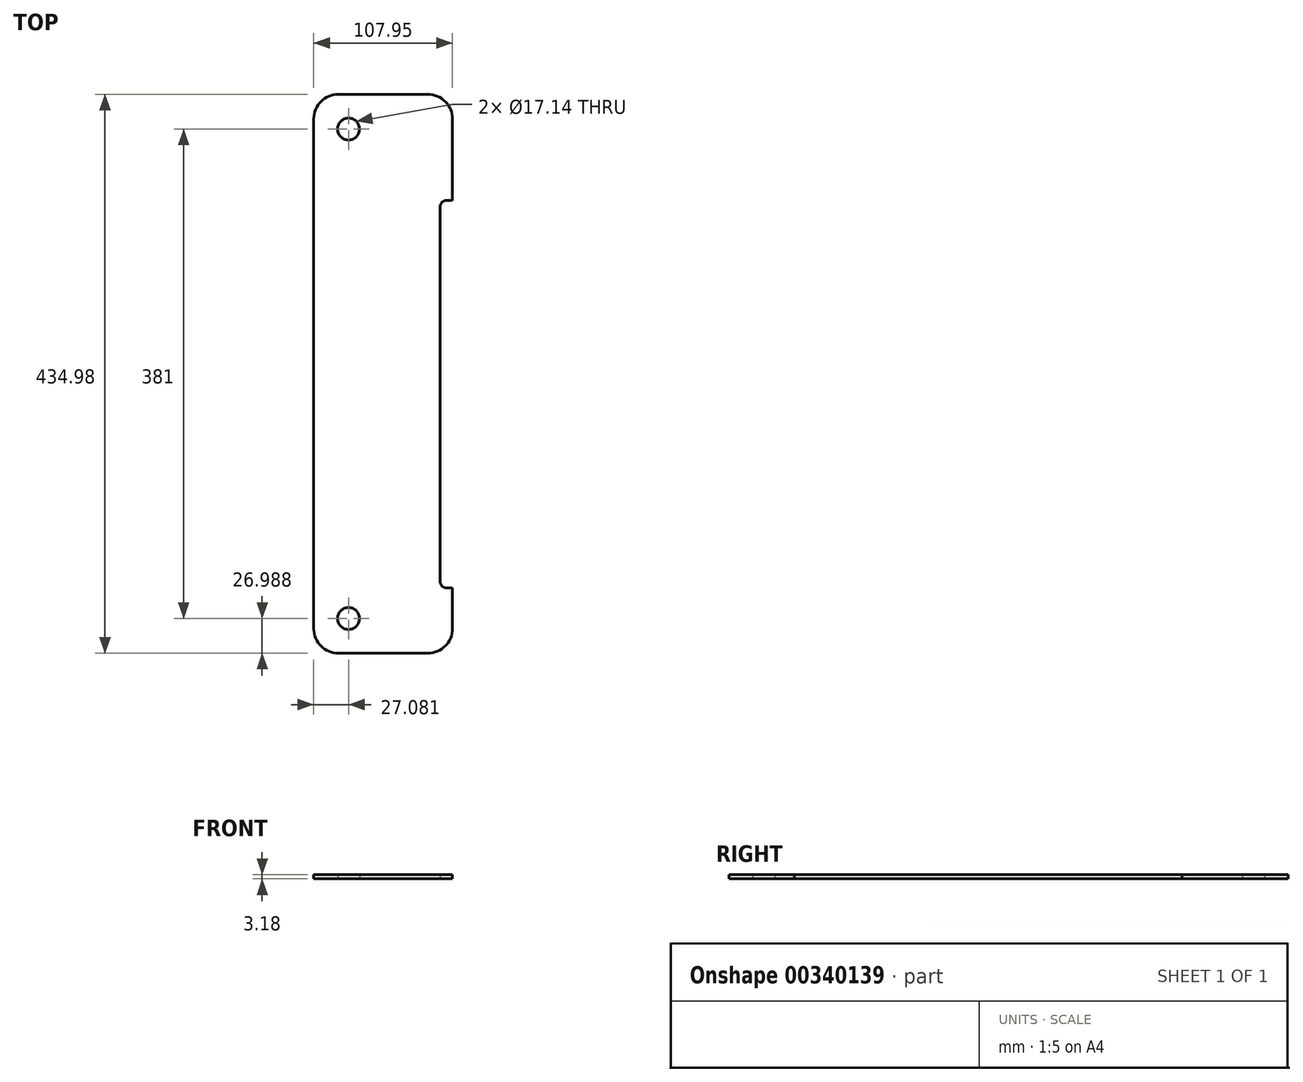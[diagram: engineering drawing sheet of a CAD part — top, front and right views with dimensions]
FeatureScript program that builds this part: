
annotation { "Feature Type Name" : "Feature", "Feature Type Description" : "" }
export const myFeature = defineFeature(function(context is Context, id is Id, definition is map)
    precondition{}
    {
        {
            var Q0;
            Q0=qCreatedBy(makeId("Top.planeOp"),FACE);
            var sketch = newSketch(context, id + "F0", { "sketchPlane" : qUnion([Q0])});
            skLineSegment(sketch, "E0.bottom", {"start": v(-130.08, 214.6) * mm, "end": v(-22.13, 214.6) * mm});
            skLineSegment(sketch, "E0.top", {"start": v(-130.08, -220.38) * mm, "end": v(-22.13, -220.38) * mm});
            skLineSegment(sketch, "E0.left", {"start": v(-130.08, 214.6) * mm, "end": v(-130.08, -220.38) * mm});
            skLineSegment(sketch, "E0.right", {"start": v(-22.13, 214.6) * mm, "end": v(-22.13, 132.05) * mm});
            skLineSegment(sketch, "E1", {"start": v(-22.13, 132.05) * mm, "end": v(-31.65, 132.05) * mm});
            skLineSegment(sketch, "E2", {"start": v(-31.65, 132.05) * mm, "end": v(-31.65, -169.58) * mm});
            skLineSegment(sketch, "E3", {"start": v(-31.65, -169.58) * mm, "end": v(-22.13, -169.58) * mm});
            skLineSegment(sketch, "E4.trimOffspring", {"start": v(-22.13, -169.58) * mm, "end": v(-22.13, -220.38) * mm});
            skPoint(sketch, "E5", {"position": v(-76.1, -220.38) * mm});
            skLineSegment(sketch, "E6", {"start": v(-130.08, 214.6) * mm, "end": v(-130.08, 160.62) * mm, "construction": true});
            skLineSegment(sketch, "E7", {"start": v(-130.08, -220.38) * mm, "end": v(-130.08, -166.4) * mm, "construction": true});
            skPoint(sketch, "E8.centerSnap0", {"position": v(-76.1, 214.6) * mm});
            skPoint(sketch, "E9", {"position": v(-103, 214.6) * mm});
            skPoint(sketch, "E10", {"position": v(-130.08, 187.6) * mm});
            skPoint(sketch, "E11", {"position": v(-130.08, -193.4) * mm});
            skPoint(sketch, "E12", {"position": v(-103, -220.38) * mm});
            skCircle(sketch, "E13", {"center": v(-103, 187.6) * mm, "radius": 8.57 * mm});
            skCircle(sketch, "E14", {"center": v(-103, -193.4) * mm, "radius": 8.57 * mm});
            skSolve(sketch);
        }
        {
            var Q0;
            Q0=qSketchRegion(id+"F0",true);
            extrude(context, id + "F1", {"entities" : qUnion([Q0]), "depth" : 3.17 * mm});
        }
        {
            var Q0;
            Q0=makeQuery(id+"F1.opExtrude","SWEPT_EDGE",EDGE,{"disambiguationData":[OSD([sQuery(id+"F0.wireOp",EDGE,"E0.top"),sQuery(id+"F0.wireOp",EDGE,"E0.left")])]});
            var Q1;
            Q1=makeQuery(id+"F1.opExtrude","SWEPT_EDGE",EDGE,{"disambiguationData":[OSD([sQuery(id+"F0.wireOp",EDGE,"E0.top"),sQuery(id+"F0.wireOp",EDGE,"E4.trimOffspring")])]});
            var Q2;
            Q2=makeQuery(id+"F1.opExtrude","SWEPT_EDGE",EDGE,{"disambiguationData":[OSD([sQuery(id+"F0.wireOp",EDGE,"E0.bottom"),sQuery(id+"F0.wireOp",EDGE,"E0.left")])]});
            var Q3;
            Q3=makeQuery(id+"F1.opExtrude","SWEPT_EDGE",EDGE,{"disambiguationData":[OSD([sQuery(id+"F0.wireOp",EDGE,"E0.top"),sQuery(id+"F0.wireOp",EDGE,"E0.left")])]});
            var Q4;
            Q4=makeQuery(id+"F1.opExtrude","SWEPT_EDGE",EDGE,{"disambiguationData":[OSD([sQuery(id+"F0.wireOp",EDGE,"E0.bottom"),sQuery(id+"F0.wireOp",EDGE,"E0.right")])]});
            fillet(context, id + "F2", {"entities" : qUnion([Q0, Q1, Q2, Q3, Q4]), "radius" : 19.05 * mm, "tangentPropagation" : true, "allowEdgeOverflow" : false});
        }
        {
            var Q0;
            Q0=makeQuery(id+"F1.opExtrude","SWEPT_EDGE",EDGE,{"disambiguationData":[OSD([sQuery(id+"F0.wireOp",EDGE,"E2"),sQuery(id+"F0.wireOp",EDGE,"E3")])]});
            var Q1;
            Q1=makeQuery(id+"F1.opExtrude","SWEPT_EDGE",EDGE,{"disambiguationData":[OSD([sQuery(id+"F0.wireOp",EDGE,"E1"),sQuery(id+"F0.wireOp",EDGE,"E2")])]});
            fillet(context, id + "F3", {"entities" : qUnion([Q0, Q1]), "radius" : 4.76 * mm, "tangentPropagation" : true, "allowEdgeOverflow" : false});
        }
    });
